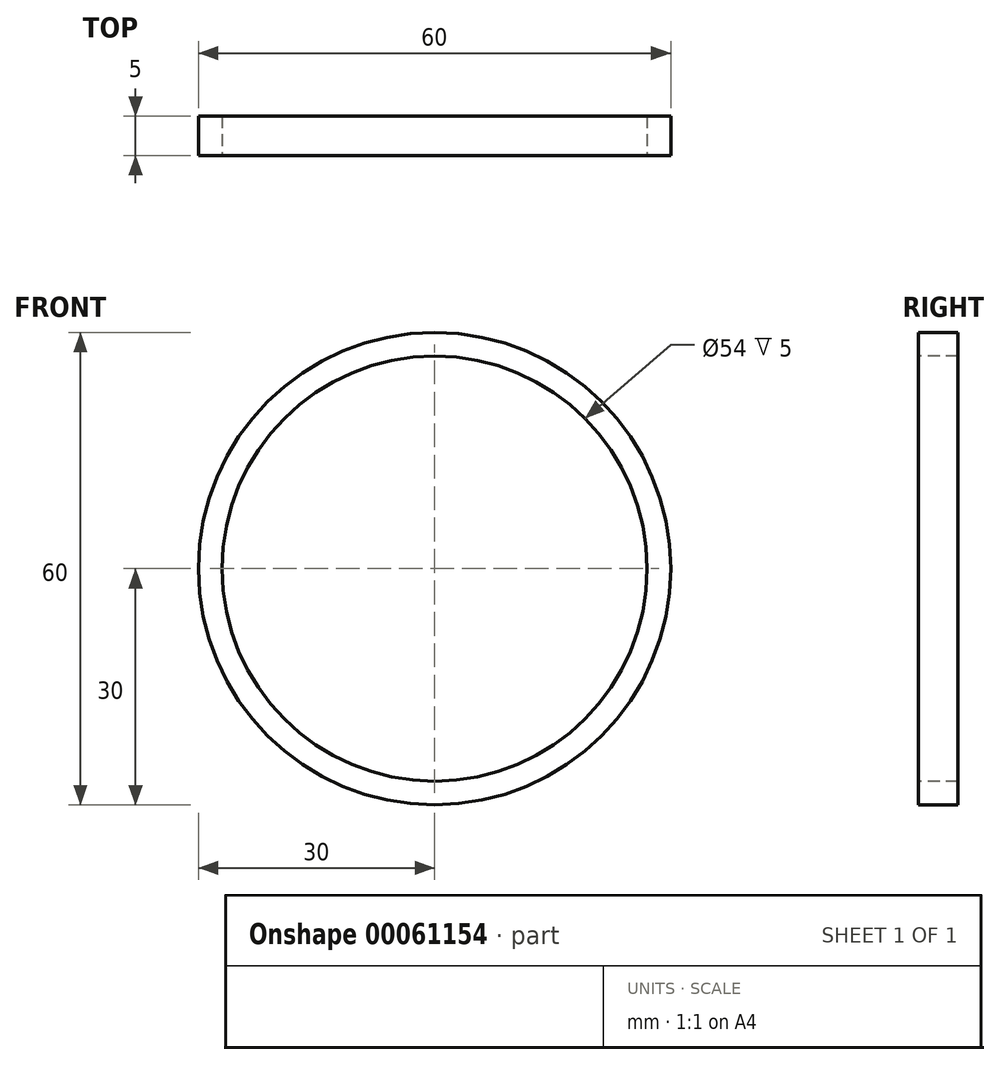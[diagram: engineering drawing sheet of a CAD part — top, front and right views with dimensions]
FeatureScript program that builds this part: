
annotation { "Feature Type Name" : "Feature", "Feature Type Description" : "" }
export const myFeature = defineFeature(function(context is Context, id is Id, definition is map)
    precondition{}
    {
        {
            var Q0;
            Q0=qCreatedBy(makeId("Front.planeOp"),FACE);
            var sketch = newSketch(context, id + "F2", { "sketchPlane" : qUnion([Q0])});
            skCircle(sketch, "E0", {"center": v(0, 0) * mm, "radius": 30 * mm});
            skCircle(sketch, "E1", {"center": v(0, 0) * mm, "radius": 27 * mm});
            skSolve(sketch);
        }
        {
            var Q0;
            Q0 = qSketchRegion(id + "F2", true);
            var Q1;
            Q1=makeQuery(id+"F2.imprint","IMPRINT",FACE,{"disambiguationData":[TD([[makeQuery(id+"F2.imprint","IMPRINT",EDGE,{"derivedFrom":sQuery(id+"F2.wireOp",EDGE,"E0")}),1.0]])]});
            extrude(context, id + "F0", {"entities" : qUnion([Q0, Q1]), "oppositeDirection" : true, "depth" : 5 * mm});
        }
    });
